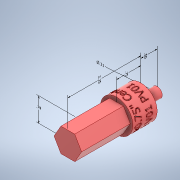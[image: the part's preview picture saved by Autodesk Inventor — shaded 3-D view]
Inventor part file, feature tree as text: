
AUTODESK INVENTOR PART (.ipt)
format: ipt  version: 2022.2 (Build 262287000, 287)  size: 1,382,912 bytes
history: native  units: in
note: dims shown in document units (in); Inventor stores cm internally (conversion verified against a paired STEP export)
features: other x7, sketch x4, extrude x3, plane x1, emboss x1
ambient origin geometry x8: Origin, YZ Plane, XZ Plane, XY Plane, X Axis, Y Axis, Z Axis, Center Point
bodies: Solid1 (feature_tree)
feature tree (16):
  other  "Annotations"
  extrude  "Hex Portion"  Depth=0.75in TaperAngle=0.0deg
  extrude  "Extrusion2"  Depth=0.75in TaperAngle=0.0deg
  other  "Reduce Size of Hex Shaft"
  extrude  "Extrusion3"  Depth=0.315in
  plane  "Work Plane1"
  emboss  "Emboss1"
  sketch  "Sketch1"  dims[d0=0.75in d1=1.5in d2=0.0in]
  sketch  "Sketch2"  dims[d3=1.0in d4=0.75in d5=0.0in]
  sketch  "Sketch3"  dims[d6=0.0075in d7=0.005in d14=0.315in]
  sketch  "Sketch4"  dims[d16=0.5in d17=0.0in d21=0.1in d22=0.0in d10=2.25in d11=0.2621in d12=0.2706in d13=0.735in d15=0.75in d18=0.5in d19=2.4445in d20=0.315in]
  other  "Linear Dimension 1"
  other  "Linear Dimension 2"
  other  "Linear Dimension 3"
  other  "Linear Dimension 4"
  other  "Diameter Dimension 1"
